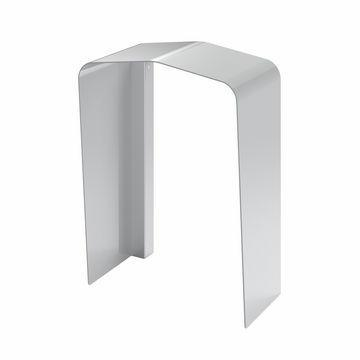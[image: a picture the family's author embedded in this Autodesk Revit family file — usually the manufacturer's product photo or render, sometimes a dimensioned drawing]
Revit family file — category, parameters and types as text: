
# Revit family: Building-RicaricaVeicoliElettrici-GEWISS-JOINON-ICON_SUPPORTO-PROTEZIONE
name_source: partatom
category: Apparecchi elettrici
units: mm (PartAtom-declared; Revit-internal decimal feet)

## family parameters
Condiviso = No
Host = Superficie
Mantenere orientamento annotazione = Sì
Punto di calcolo locali = Sì
Quota connettore circolare = Usa diametro
Taglio con vuoti quando caricato = No
Tipo di parte = Normale

## types (1)
- GWJ8104 - SUPPORTO PROTEZIONE I-CON
    Adatto per = WallBox I-CON
    BLOCCO = B=C
    Catalogo = E-MOBILITY
    Codice EAN = 8034035071393
    Codice Electrocod = 2242
    Descrizione = SUPPORTO PROTEZIONE I-CON
    Descrizione: = Supporto protezione I-CON
    FORMULA = 1000 mm  [stored 3.28084 ft]
    IDF = 2af7dd89-743f-435f-ac6f-e7531f5fa199
    IDT = de4cf1b2-9fd5-41ee-a883-306328bc9e16
    Immagine tipo = ICON_TETTUCCIO.jpg
    L = 155 mm  [stored 0.50853 ft]
    Modello = GWJ8104
    N.poli = 1
    POMELLO = bianco
    PRESA = Giallo
    Produttore = GEWISS S.p.A.
    Prospetto di default = 1219 mm
    STRUTTURA = RAL - 7035
    STRUTTURA ALTA = blue
    Scheda Tecnica = https://www.gewiss.com
    Spostamento_S = 1500 mm  [stored 4.92126 ft]
    URL = https://www.gewiss.com
    VETRO = Vetro
    Versione file RFA = 19.4
    Voltaggio = 0 V
    W = 115 mm  [stored 0.377297 ft]

note: [stored X ft] marks values corroborated as IEEE doubles in the binary element streams (Revit-internal decimal feet)
